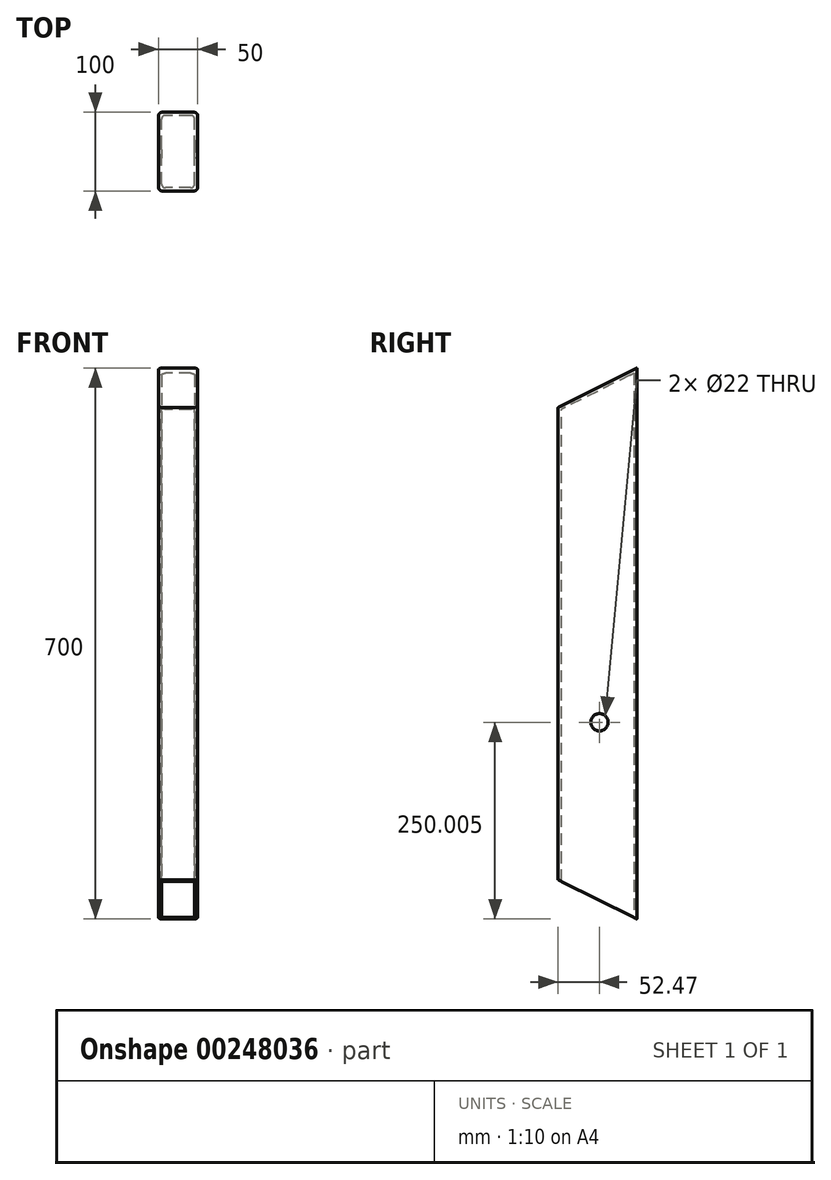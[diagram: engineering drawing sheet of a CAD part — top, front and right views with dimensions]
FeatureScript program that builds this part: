
annotation { "Feature Type Name" : "Feature", "Feature Type Description" : "" }
export const myFeature = defineFeature(function(context is Context, id is Id, definition is map)
    precondition{}
    {
        {
            var Q0;
            Q0=qCreatedBy(makeId("Right.planeOp"),FACE);
            var sketch = newSketch(context, id + "F0", { "sketchPlane" : qUnion([Q0])});
            skPoint(sketch, "E0.middle", {"position": v(0, 0) * mm});
            skPoint(sketch, "E1", {"position": v(0, -125.83) * mm});
            skPoint(sketch, "E2", {"position": v(-52.47, -325.83) * mm});
            skPoint(sketch, "E3.orphan", {"position": v(47.53, -375.83) * mm});
            skLineSegment(sketch, "E4", {"start": v(-52.47, -325.83) * mm, "end": v(47.53, -375.83) * mm});
            skLineSegment(sketch, "E5", {"start": v(47.53, 324.17) * mm, "end": v(47.53, -375.83) * mm});
            skLineSegment(sketch, "E6", {"start": v(-52.47, -325.83) * mm, "end": v(-52.47, 274.17) * mm});
            skPoint(sketch, "E7", {"position": v(47.53, -275.83) * mm});
            skLineSegment(sketch, "E8", {"start": v(47.53, 324.17) * mm, "end": v(-52.47, 274.17) * mm});
            skSolve(sketch);
        }
        {
            var Q0;
            Q0=makeQuery(id+"F0.imprint","IMPRINT",FACE,{"disambiguationData":[TD([[makeQuery(id+"F0.imprint","IMPRINT",EDGE,{"derivedFrom":sQuery(id+"F0.wireOp",EDGE,"E4")}),1.0]])]});
            extrude(context, id + "F1", {"entities" : qUnion([Q0]), "depth" : 50 * mm});
        }
        {
            var Q0;
            Q0=makeQuery(id+"F1.opExtrude","SWEPT_FACE",FACE,{"disambiguationData":[OSD([sQuery(id+"F0.wireOp",EDGE,"E4")])]});
            shell(context, id + "F2", {"entities" : qUnion([Q0]), "thickness" : 4 * mm});
        }
        {
            var Q0;
            Q0=makeQuery(id+"F1.opExtrude","CAP_EDGE",EDGE,{"disambiguationData":[OSD([sQuery(id+"F0.wireOp",EDGE,"E6")])],"isStart":false});
            var Q1;
            Q1=makeQuery(id+"F1.opExtrude","CAP_EDGE",EDGE,{"disambiguationData":[OSD([sQuery(id+"F0.wireOp",EDGE,"E5")])],"isStart":false});
            var Q2;
            Q2=makeQuery(id+"F1.opExtrude","CAP_EDGE",EDGE,{"disambiguationData":[OSD([sQuery(id+"F0.wireOp",EDGE,"E5")])],"isStart":true});
            var Q3;
            Q3=makeQuery(id+"F1.opExtrude","CAP_EDGE",EDGE,{"disambiguationData":[OSD([sQuery(id+"F0.wireOp",EDGE,"E6")])],"isStart":true});
            var Q4;
            {var subQ0=sQuery(id+"F0.wireOp",EDGE,"E6");Q4=makeQuery(id+"F2.opShell","OFFSET_EDGE",EDGE,{"disambiguationData":[OSD([subQ0]),TDD([makeQuery(id+"F1.opExtrude","CAP_EDGE",EDGE,{"disambiguationData":[OSD([subQ0])],"isStart":true})])]});}
            var Q5;
            {var subQ0=sQuery(id+"F0.wireOp",EDGE,"E5");Q5=makeQuery(id+"F2.opShell","OFFSET_EDGE",EDGE,{"disambiguationData":[OSD([subQ0]),TDD([makeQuery(id+"F1.opExtrude","CAP_EDGE",EDGE,{"disambiguationData":[OSD([subQ0])],"isStart":true})])]});}
            var Q6;
            {var subQ0=sQuery(id+"F0.wireOp",EDGE,"E5");Q6=makeQuery(id+"F2.opShell","OFFSET_EDGE",EDGE,{"disambiguationData":[OSD([subQ0]),TDD([makeQuery(id+"F1.opExtrude","CAP_EDGE",EDGE,{"disambiguationData":[OSD([subQ0])],"isStart":false})])]});}
            var Q7;
            {var subQ0=sQuery(id+"F0.wireOp",EDGE,"E6");Q7=makeQuery(id+"F2.opShell","OFFSET_EDGE",EDGE,{"disambiguationData":[OSD([subQ0]),TDD([makeQuery(id+"F1.opExtrude","CAP_EDGE",EDGE,{"disambiguationData":[OSD([subQ0])],"isStart":false})])]});}
            fillet(context, id + "F3", {"entities" : qUnion([Q0, Q1, Q2, Q3, Q4, Q5, Q6, Q7]), "radius" : 5 * mm, "tangentPropagation" : true, "allowEdgeOverflow" : false});
        }
        {
            var Q0;
            Q0=sQuery(id+"F0.wireOp",VERTEX,"E1");
            var Q1;
            Q1=makeQuery(id+"F1.opExtrude","SWEPT_BODY",BODY,{"disambiguationData":[OSD([sQuery(id+"F0.wireOp",EDGE,"E4"),sQuery(id+"F0.wireOp",EDGE,"E5"),sQuery(id+"F0.wireOp",EDGE,"E6"),sQuery(id+"F0.wireOp",EDGE,"E8")])]});
            hole(context, id + "F4", {"style" : HoleStyle.SIMPLE, "endStyle" : HoleEndStyle.THROUGH, "oppositeDirection" : true, "holeDiameter" : 22 * mm, "tappedDepth" : 12 * mm, "tapClearance" : 3, "locations" : qUnion([Q0]), "scope" : qUnion([Q1])});
        }
    });
